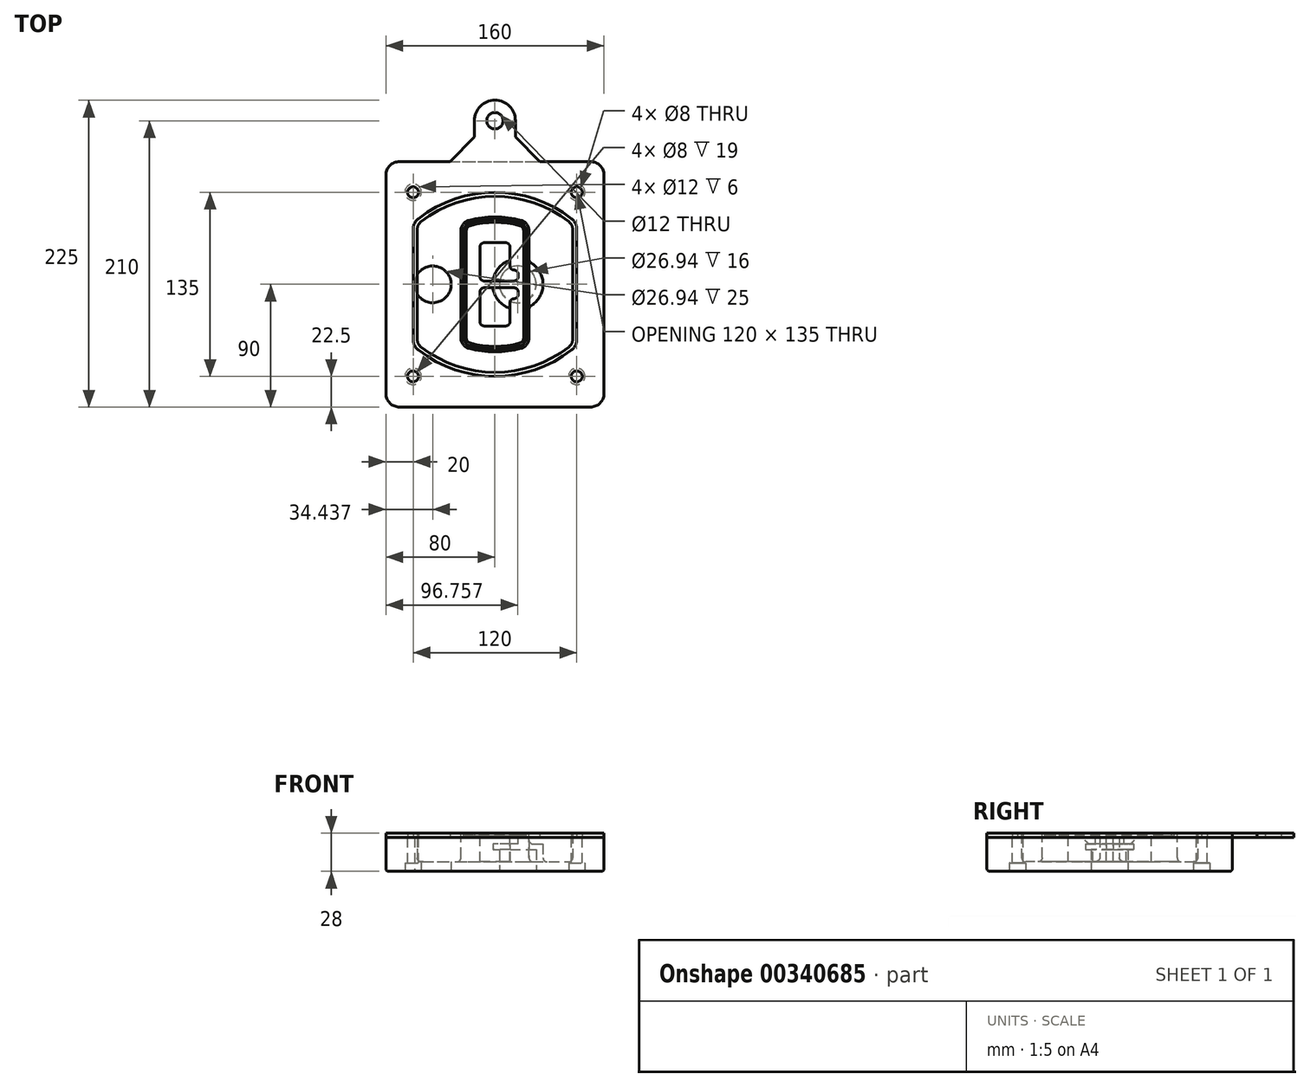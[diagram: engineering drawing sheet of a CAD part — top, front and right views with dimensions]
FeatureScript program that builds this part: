
annotation { "Feature Type Name" : "Feature", "Feature Type Description" : "" }
export const myFeature = defineFeature(function(context is Context, id is Id, definition is map)
    precondition{}
    {
        {
            var Q0;
            Q0=qCreatedBy(makeId("Top.planeOp"),FACE);
            var sketch = newSketch(context, id + "F0", { "sketchPlane" : qUnion([Q0])});
            skPoint(sketch, "E0.rect.middle", {"position": v(0, 0) * mm});
            skLineSegment(sketch, "E1.bottom", {"start": v(-70, -90) * mm, "end": v(70, -90) * mm});
            skLineSegment(sketch, "E1.top", {"start": v(-70, 90) * mm, "end": v(70, 90) * mm});
            skLineSegment(sketch, "E1.left", {"start": v(-80, -80) * mm, "end": v(-80, 80) * mm});
            skLineSegment(sketch, "E1.right", {"start": v(80, -80) * mm, "end": v(80, 80) * mm});
            skLineSegment(sketch, "E2", {"start": v(-80, 90) * mm, "end": v(80, -90) * mm, "construction": true});
            skLineSegment(sketch, "E3", {"start": v(80, 90) * mm, "end": v(-80, -90) * mm, "construction": true});
            skCircle(sketch, "E4", {"center": v(-60, 67.5) * mm, "radius": 4 * mm});
            skCircle(sketch, "E5", {"center": v(60, 67.5) * mm, "radius": 4 * mm});
            skCircle(sketch, "E6", {"center": v(60, -67.5) * mm, "radius": 4 * mm});
            skCircle(sketch, "E7", {"center": v(-60, -67.5) * mm, "radius": 4 * mm});
            skLineSegment(sketch, "E8", {"start": v(-60, 67.5) * mm, "end": v(60, 67.5) * mm, "construction": true});
            skLineSegment(sketch, "E9", {"start": v(60, 67.5) * mm, "end": v(60, -67.5) * mm, "construction": true});
            skLineSegment(sketch, "E10", {"start": v(60, -67.5) * mm, "end": v(-60, -67.5) * mm, "construction": true});
            skLineSegment(sketch, "E11", {"start": v(-60, -67.5) * mm, "end": v(-60, 67.5) * mm, "construction": true});
            skLineSegment(sketch, "E12", {"start": v(-60, 40.3) * mm, "end": v(-60, -40.3) * mm});
            skLineSegment(sketch, "E13", {"start": v(60, 40.3) * mm, "end": v(60, -40.3) * mm});
            skArc(sketch, "E14", {"start": v(56.15, 48.18) * mm, "mid": v(0, 67.5) * mm, "end": v(-56.15, 48.18) * mm});
            skArc(sketch, "E15", {"start": v(-56.15, -48.18) * mm, "mid": v(0, -67.5) * mm, "end": v(56.15, -48.18) * mm});
            skLineSegment(sketch, "E16", {"start": v(-60, 0) * mm, "end": v(60, 0) * mm, "construction": true});
            skPoint(sketch, "E17.visualSharp", {"position": v(-60, -45) * mm});
            skArc(sketch, "E17.filletArc", {"start": v(-60, -40.3) * mm, "mid": v(-58.99, -44.68) * mm, "end": v(-56.15, -48.18) * mm});
            skPoint(sketch, "E18.visualSharp", {"position": v(-60, 45) * mm});
            skArc(sketch, "E18.filletArc", {"start": v(-56.15, 48.18) * mm, "mid": v(-58.99, 44.68) * mm, "end": v(-60, 40.3) * mm});
            skPoint(sketch, "E19.visualSharp", {"position": v(60, 45) * mm});
            skArc(sketch, "E19.filletArc", {"start": v(60, 40.3) * mm, "mid": v(58.99, 44.68) * mm, "end": v(56.15, 48.18) * mm});
            skPoint(sketch, "E20.visualSharp", {"position": v(60, -45) * mm});
            skArc(sketch, "E20.filletArc", {"start": v(56.15, -48.18) * mm, "mid": v(58.99, -44.68) * mm, "end": v(60, -40.3) * mm});
            skPoint(sketch, "E21.visualSharp", {"position": v(-80, 90) * mm});
            skArc(sketch, "E21.filletArc", {"start": v(-70, 90) * mm, "mid": v(-77.07, 87.07) * mm, "end": v(-80, 80) * mm});
            skPoint(sketch, "E22.visualSharp", {"position": v(80, 90) * mm});
            skArc(sketch, "E22.filletArc", {"start": v(80, 80) * mm, "mid": v(77.07, 87.07) * mm, "end": v(70, 90) * mm});
            skPoint(sketch, "E23.visualSharp", {"position": v(80, -90) * mm});
            skArc(sketch, "E23.filletArc", {"start": v(70, -90) * mm, "mid": v(77.07, -87.07) * mm, "end": v(80, -80) * mm});
            skPoint(sketch, "E24.visualSharp", {"position": v(-80, -90) * mm});
            skArc(sketch, "E24.filletArc", {"start": v(-80, -80) * mm, "mid": v(-77.07, -87.07) * mm, "end": v(-70, -90) * mm});
            skArc(sketch, "E25.0", {"start": v(57, 40.3) * mm, "mid": v(56.3, 43.36) * mm, "end": v(54.3, 45.81) * mm});
            skLineSegment(sketch, "E25.1", {"start": v(57, 40.3) * mm, "end": v(57, -40.3) * mm});
            skArc(sketch, "E25.2", {"start": v(54.3, -45.81) * mm, "mid": v(56.3, -43.36) * mm, "end": v(57, -40.3) * mm});
            skArc(sketch, "E25.3", {"start": v(-54.3, -45.81) * mm, "mid": v(0, -64.5) * mm, "end": v(54.3, -45.81) * mm});
            skArc(sketch, "E25.4", {"start": v(-57, -40.3) * mm, "mid": v(-56.3, -43.36) * mm, "end": v(-54.3, -45.81) * mm});
            skArc(sketch, "E25.5", {"start": v(54.3, 45.81) * mm, "mid": v(0, 64.5) * mm, "end": v(-54.3, 45.81) * mm});
            skLineSegment(sketch, "E25.6", {"start": v(-57, 40.3) * mm, "end": v(-57, -40.3) * mm});
            skArc(sketch, "E25.7", {"start": v(-54.3, 45.81) * mm, "mid": v(-56.3, 43.36) * mm, "end": v(-57, 40.3) * mm});
            skArc(sketch, "E26.0", {"start": v(-58.62, 51.33) * mm, "mid": v(-62.58, 46.43) * mm, "end": v(-64, 40.3) * mm});
            skArc(sketch, "E26.1", {"start": v(58.62, 51.33) * mm, "mid": v(0, 71.5) * mm, "end": v(-58.62, 51.33) * mm});
            skArc(sketch, "E26.2", {"start": v(64, 40.3) * mm, "mid": v(62.58, 46.43) * mm, "end": v(58.62, 51.33) * mm});
            skLineSegment(sketch, "E26.3", {"start": v(64, 40.3) * mm, "end": v(64, -40.3) * mm});
            skArc(sketch, "E26.4", {"start": v(58.62, -51.33) * mm, "mid": v(62.58, -46.43) * mm, "end": v(64, -40.3) * mm});
            skLineSegment(sketch, "E26.5", {"start": v(-64, 40.3) * mm, "end": v(-64, -40.3) * mm});
            skArc(sketch, "E26.6", {"start": v(-58.62, -51.33) * mm, "mid": v(0, -71.5) * mm, "end": v(58.62, -51.33) * mm});
            skArc(sketch, "E26.7", {"start": v(-64, -40.3) * mm, "mid": v(-62.58, -46.43) * mm, "end": v(-58.62, -51.33) * mm});
            skSolve(sketch);
        }
        {
            var Q0;
            Q0=makeQuery(id+"F0.imprint","IMPRINT",FACE,{"disambiguationData":[TD([[makeQuery(id+"F0.imprint","IMPRINT",EDGE,{"derivedFrom":sQuery(id+"F0.wireOp",EDGE,"E1.bottom")}),1.0]])]});
            var Q1;
            Q1=makeQuery(id+"F0.imprint","IMPRINT",FACE,{"disambiguationData":[TD([[makeQuery(id+"F0.imprint","IMPRINT",EDGE,{"derivedFrom":sQuery(id+"F0.wireOp",EDGE,"E12")}),1.0]])]});
            var Q2;
            Q2=makeQuery(id+"F0.imprint","IMPRINT",FACE,{"disambiguationData":[TD([[makeQuery(id+"F0.imprint","IMPRINT",EDGE,{"derivedFrom":sQuery(id+"F0.wireOp",EDGE,"E25.0")}),1.0]])]});
            var Q3;
            Q3=makeQuery(id+"F0.imprint","IMPRINT",FACE,{"disambiguationData":[TD([[makeQuery(id+"F0.imprint","IMPRINT",EDGE,{"derivedFrom":sQuery(id+"F0.wireOp",EDGE,"E12")}),-1.0]])]});
            extrude(context, id + "F1", {"entities" : qUnion([Q0, Q1, Q2, Q3]), "oppositeDirection" : true, "depth" : 25 * mm});
        }
        {
            var Q0;
            Q0=makeQuery(id+"F0.imprint","IMPRINT",FACE,{"disambiguationData":[TD([[makeQuery(id+"F0.imprint","IMPRINT",EDGE,{"derivedFrom":sQuery(id+"F0.wireOp",EDGE,"E12")}),1.0]])]});
            extrude(context, id + "F2", {"entities" : qUnion([Q0]), "operationType" : NewBodyOperationType.ADD, "depth" : 3 * mm});
        }
        {
            var Q0;
            Q0=makeQuery(id+"F0.imprint","IMPRINT",FACE,{"disambiguationData":[TD([[makeQuery(id+"F0.imprint","IMPRINT",EDGE,{"derivedFrom":sQuery(id+"F0.wireOp",EDGE,"E25.0")}),1.0]])]});
            extrude(context, id + "F3", {"entities" : qUnion([Q0]), "operationType" : NewBodyOperationType.REMOVE, "oppositeDirection" : true, "depth" : 18 * mm});
        }
        {
            var Q0;
            Q0=makeQuery(id+"F2.opExtrude","CAP_FACE",FACE,{"disambiguationData":[OSD([sQuery(id+"F0.wireOp",EDGE,"E12"),sQuery(id+"F0.wireOp",EDGE,"E13"),sQuery(id+"F0.wireOp",EDGE,"E14"),sQuery(id+"F0.wireOp",EDGE,"E15"),sQuery(id+"F0.wireOp",EDGE,"E17.filletArc"),sQuery(id+"F0.wireOp",EDGE,"E18.filletArc"),sQuery(id+"F0.wireOp",EDGE,"E19.filletArc"),sQuery(id+"F0.wireOp",EDGE,"E20.filletArc"),sQuery(id+"F0.wireOp",EDGE,"E25.0"),sQuery(id+"F0.wireOp",EDGE,"E25.1"),sQuery(id+"F0.wireOp",EDGE,"E25.2"),sQuery(id+"F0.wireOp",EDGE,"E25.3"),sQuery(id+"F0.wireOp",EDGE,"E25.4"),sQuery(id+"F0.wireOp",EDGE,"E25.5"),sQuery(id+"F0.wireOp",EDGE,"E25.6"),sQuery(id+"F0.wireOp",EDGE,"E25.7")])],"isStart":false});
            var sketch = newSketch(context, id + "F4", { "sketchPlane" : qUnion([Q0])});
            skArc(sketch, "E27.0", {"start": v(-19.08, -46.97) * mm, "mid": v(0, -49.5) * mm, "end": v(19.08, -46.97) * mm});
            skArc(sketch, "E28.0", {"start": v(19.08, 46.97) * mm, "mid": v(0, 49.5) * mm, "end": v(-19.08, 46.97) * mm});
            skLineSegment(sketch, "E29", {"start": v(-25, 39.25) * mm, "end": v(-25, -39.25) * mm});
            skLineSegment(sketch, "E30", {"start": v(25, 39.25) * mm, "end": v(25, -39.25) * mm});
            skLineSegment(sketch, "E31", {"start": v(-25, 45.1) * mm, "end": v(25, 45.1) * mm, "construction": true});
            skLineSegment(sketch, "E32", {"start": v(-25, -45.1) * mm, "end": v(25, -45.1) * mm, "construction": true});
            skPoint(sketch, "E33.visualSharp", {"position": v(-25, 45.1) * mm});
            skArc(sketch, "E33.filletArc", {"start": v(-19.08, 46.97) * mm, "mid": v(-23.35, 44.11) * mm, "end": v(-25, 39.25) * mm});
            skPoint(sketch, "E34.visualSharp", {"position": v(25, 45.1) * mm});
            skArc(sketch, "E34.filletArc", {"start": v(25, 39.25) * mm, "mid": v(23.35, 44.11) * mm, "end": v(19.08, 46.97) * mm});
            skPoint(sketch, "E35.visualSharp", {"position": v(25, -45.1) * mm});
            skArc(sketch, "E35.filletArc", {"start": v(19.08, -46.97) * mm, "mid": v(23.35, -44.11) * mm, "end": v(25, -39.25) * mm});
            skPoint(sketch, "E36.visualSharp", {"position": v(-25, -45.1) * mm});
            skArc(sketch, "E36.filletArc", {"start": v(-25, -39.25) * mm, "mid": v(-23.35, -44.11) * mm, "end": v(-19.08, -46.97) * mm});
            skArc(sketch, "E37.0", {"start": v(54.3, 45.81) * mm, "mid": v(0, 64.5) * mm, "end": v(-54.3, 45.81) * mm});
            skArc(sketch, "E37.1", {"start": v(-54.3, 45.81) * mm, "mid": v(-56.3, 43.36) * mm, "end": v(-57, 40.3) * mm});
            skLineSegment(sketch, "E37.2", {"start": v(-57, 40.3) * mm, "end": v(-57, -40.3) * mm});
            skArc(sketch, "E37.3", {"start": v(-57, -40.3) * mm, "mid": v(-56.3, -43.36) * mm, "end": v(-54.3, -45.81) * mm});
            skArc(sketch, "E37.4", {"start": v(-54.3, -45.81) * mm, "mid": v(0, -64.5) * mm, "end": v(54.3, -45.81) * mm});
            skArc(sketch, "E37.5", {"start": v(54.3, -45.81) * mm, "mid": v(56.3, -43.36) * mm, "end": v(57, -40.3) * mm});
            skLineSegment(sketch, "E37.6", {"start": v(57, 40.3) * mm, "end": v(57, -40.3) * mm});
            skArc(sketch, "E37.7", {"start": v(57, 40.3) * mm, "mid": v(56.3, 43.36) * mm, "end": v(54.3, 45.81) * mm});
            skLineSegment(sketch, "E38.0", {"start": v(23, 39.25) * mm, "end": v(23, -39.25) * mm});
            skArc(sketch, "E38.1", {"start": v(18.56, -45.04) * mm, "mid": v(21.76, -42.9) * mm, "end": v(23, -39.25) * mm});
            skArc(sketch, "E38.2", {"start": v(-18.56, -45.04) * mm, "mid": v(0, -47.5) * mm, "end": v(18.56, -45.04) * mm});
            skArc(sketch, "E38.3", {"start": v(-23, -39.25) * mm, "mid": v(-21.76, -42.9) * mm, "end": v(-18.56, -45.04) * mm});
            skLineSegment(sketch, "E38.4", {"start": v(-23, 39.25) * mm, "end": v(-23, -39.25) * mm});
            skArc(sketch, "E38.5", {"start": v(23, 39.25) * mm, "mid": v(21.76, 42.9) * mm, "end": v(18.56, 45.04) * mm});
            skArc(sketch, "E38.6", {"start": v(-18.56, 45.04) * mm, "mid": v(-21.76, 42.9) * mm, "end": v(-23, 39.25) * mm});
            skArc(sketch, "E38.7", {"start": v(18.56, 45.04) * mm, "mid": v(0, 47.5) * mm, "end": v(-18.56, 45.04) * mm});
            skArc(sketch, "E39.0", {"start": v(21, 39.25) * mm, "mid": v(20.18, 41.68) * mm, "end": v(18.04, 43.1) * mm});
            skLineSegment(sketch, "E39.1", {"start": v(21, 39.25) * mm, "end": v(21, -39.25) * mm});
            skArc(sketch, "E39.2", {"start": v(18.04, -43.1) * mm, "mid": v(20.18, -41.68) * mm, "end": v(21, -39.25) * mm});
            skArc(sketch, "E39.3", {"start": v(-18.04, -43.1) * mm, "mid": v(0, -45.5) * mm, "end": v(18.04, -43.1) * mm});
            skArc(sketch, "E39.4", {"start": v(-21, -39.25) * mm, "mid": v(-20.18, -41.68) * mm, "end": v(-18.04, -43.1) * mm});
            skArc(sketch, "E39.5", {"start": v(18.04, 43.1) * mm, "mid": v(0, 45.5) * mm, "end": v(-18.04, 43.1) * mm});
            skLineSegment(sketch, "E39.6", {"start": v(-21, 39.25) * mm, "end": v(-21, -39.25) * mm});
            skArc(sketch, "E39.7", {"start": v(-18.04, 43.1) * mm, "mid": v(-20.18, 41.68) * mm, "end": v(-21, 39.25) * mm});
            skLineSegment(sketch, "E40", {"start": v(-25, 0) * mm, "end": v(25, 0) * mm, "construction": true});
            skLineSegment(sketch, "E41", {"start": v(-11, 5.5) * mm, "end": v(-11, 27.5) * mm});
            skLineSegment(sketch, "E42", {"start": v(-8, 30.5) * mm, "end": v(8, 30.5) * mm});
            skLineSegment(sketch, "E43", {"start": v(11, 27.5) * mm, "end": v(11, 13.5) * mm});
            skLineSegment(sketch, "E44", {"start": v(14, 10.5) * mm, "end": v(14, 10.5) * mm});
            skLineSegment(sketch, "E45", {"start": v(17, 7.5) * mm, "end": v(17, 5.5) * mm});
            skLineSegment(sketch, "E46", {"start": v(14, 2.5) * mm, "end": v(-8, 2.5) * mm});
            skPoint(sketch, "E47.visualSharp", {"position": v(-11, 30.5) * mm});
            skArc(sketch, "E47.filletArc", {"start": v(-8, 30.5) * mm, "mid": v(-10.12, 29.62) * mm, "end": v(-11, 27.5) * mm});
            skPoint(sketch, "E48.visualSharp", {"position": v(11, 30.5) * mm});
            skArc(sketch, "E48.filletArc", {"start": v(11, 27.5) * mm, "mid": v(10.12, 29.62) * mm, "end": v(8, 30.5) * mm});
            skPoint(sketch, "E49.visualSharp", {"position": v(11, 10.5) * mm});
            skArc(sketch, "E49.filletArc", {"start": v(11, 13.5) * mm, "mid": v(11.88, 11.38) * mm, "end": v(14, 10.5) * mm});
            skPoint(sketch, "E50.visualSharp", {"position": v(17, 10.5) * mm});
            skArc(sketch, "E50.filletArc", {"start": v(17, 7.5) * mm, "mid": v(16.12, 9.62) * mm, "end": v(14, 10.5) * mm});
            skPoint(sketch, "E51.visualSharp", {"position": v(17, 2.5) * mm});
            skArc(sketch, "E51.filletArc", {"start": v(14, 2.5) * mm, "mid": v(16.12, 3.38) * mm, "end": v(17, 5.5) * mm});
            skPoint(sketch, "E52.visualSharp", {"position": v(-11, 2.5) * mm});
            skArc(sketch, "E52.filletArc", {"start": v(-11, 5.5) * mm, "mid": v(-10.12, 3.38) * mm, "end": v(-8, 2.5) * mm});
            skLineSegment(sketch, "E53.0.MirrorCS", {"start": v(14, -2.5) * mm, "end": v(-8, -2.5) * mm});
            skArc(sketch, "E54.0.MirrorCS", {"start": v(-11, -5.5) * mm, "mid": v(-10.12, -3.38) * mm, "end": v(-8, -2.5) * mm});
            skLineSegment(sketch, "E55.0.MirrorCS", {"start": v(-11, -5.5) * mm, "end": v(-11, -27.5) * mm});
            skArc(sketch, "E56.0.MirrorCS", {"start": v(-8, -30.5) * mm, "mid": v(-10.12, -29.62) * mm, "end": v(-11, -27.5) * mm});
            skLineSegment(sketch, "E57.0.MirrorCS", {"start": v(-8, -30.5) * mm, "end": v(8, -30.5) * mm});
            skArc(sketch, "E58.0.MirrorCS", {"start": v(11, -27.5) * mm, "mid": v(10.12, -29.62) * mm, "end": v(8, -30.5) * mm});
            skLineSegment(sketch, "E59.0.MirrorCS", {"start": v(11, -27.5) * mm, "end": v(11, -13.5) * mm});
            skArc(sketch, "E60.0.MirrorCS", {"start": v(11, -13.5) * mm, "mid": v(11.88, -11.38) * mm, "end": v(14, -10.5) * mm});
            skArc(sketch, "E61.0.MirrorCS", {"start": v(17, -7.5) * mm, "mid": v(16.12, -9.62) * mm, "end": v(14, -10.5) * mm});
            skLineSegment(sketch, "E62.0.MirrorCS", {"start": v(17, -7.5) * mm, "end": v(17, -5.5) * mm});
            skArc(sketch, "E63.0.MirrorCS", {"start": v(14, -2.5) * mm, "mid": v(16.12, -3.38) * mm, "end": v(17, -5.5) * mm});
            skSolve(sketch);
        }
        {
            var Q0;
            Q0=makeQuery(id+"F4.imprint","IMPRINT",FACE,{"disambiguationData":[TD([[makeQuery(id+"F4.imprint","IMPRINT",EDGE,{"derivedFrom":sQuery(id+"F4.wireOp",EDGE,"E27.0")}),1.0]])]});
            var Q1;
            Q1=makeQuery(id+"F4.imprint","IMPRINT",FACE,{"disambiguationData":[TD([[makeQuery(id+"F4.imprint","IMPRINT",EDGE,{"derivedFrom":sQuery(id+"F4.wireOp",EDGE,"E38.0")}),-1.0]])]});
            var Q2;
            Q2=makeQuery(id+"F4.imprint","IMPRINT",FACE,{"disambiguationData":[TD([[makeQuery(id+"F4.imprint","IMPRINT",EDGE,{"derivedFrom":sQuery(id+"F4.wireOp",EDGE,"E39.0")}),1.0]])]});
            extrude(context, id + "F5", {"entities" : qUnion([Q0, Q1, Q2]), "operationType" : NewBodyOperationType.ADD, "endBound" : BoundingType.UP_TO_NEXT, "oppositeDirection" : true, "depth" : 25 * mm});
        }
        {
            var Q0;
            Q0=makeQuery(id+"F4.imprint","IMPRINT",FACE,{"disambiguationData":[TD([[makeQuery(id+"F4.imprint","IMPRINT",EDGE,{"derivedFrom":sQuery(id+"F4.wireOp",EDGE,"E38.0")}),-1.0]])]});
            extrude(context, id + "F6", {"entities" : qUnion([Q0]), "operationType" : NewBodyOperationType.REMOVE, "oppositeDirection" : true, "depth" : 2 * mm});
        }
        {
            var Q0;
            Q0=makeQuery(id+"F1.opExtrude","CAP_FACE",FACE,{"disambiguationData":[OSD([sQuery(id+"F0.wireOp",EDGE,"E1.bottom"),sQuery(id+"F0.wireOp",EDGE,"E1.top"),sQuery(id+"F0.wireOp",EDGE,"E1.left"),sQuery(id+"F0.wireOp",EDGE,"E1.right"),sQuery(id+"F0.wireOp",EDGE,"E4"),sQuery(id+"F0.wireOp",EDGE,"E5"),sQuery(id+"F0.wireOp",EDGE,"E6"),sQuery(id+"F0.wireOp",EDGE,"E7"),sQuery(id+"F0.wireOp",EDGE,"E21.filletArc"),sQuery(id+"F0.wireOp",EDGE,"E22.filletArc"),sQuery(id+"F0.wireOp",EDGE,"E23.filletArc"),sQuery(id+"F0.wireOp",EDGE,"E24.filletArc")])],"isStart":false});
            var sketch = newSketch(context, id + "F7", { "sketchPlane" : qUnion([Q0])});
            skCircle(sketch, "E64", {"center": v(16.76, 0) * mm, "radius": 13.47 * mm});
            skCircle(sketch, "E65", {"center": v(-45.56, 0) * mm, "radius": 13.47 * mm});
            skLineSegment(sketch, "E66", {"start": v(80, 0) * mm, "end": v(-80, 0) * mm});
            skCircle(sketch, "E67", {"center": v(16.76, 0) * mm, "radius": 18.47 * mm});
            skCircle(sketch, "E68", {"center": v(60, -67.5) * mm, "radius": 6 * mm});
            skCircle(sketch, "E69", {"center": v(-60, -67.5) * mm, "radius": 6 * mm});
            skCircle(sketch, "E70", {"center": v(-60, 67.5) * mm, "radius": 6 * mm});
            skCircle(sketch, "E71", {"center": v(60, 67.5) * mm, "radius": 6 * mm});
            skSolve(sketch);
        }
        {
            var Q0;
            {var subQ1=sQuery(id+"F7.wireOp",EDGE,"E66");var subQ4=sQuery(id+"F7.wireOp",EDGE,"E64");var subQ6=makeQuery(id+"F7.imprint","INTERSECT",VERTEX,{"disambiguationData":[OD(0.0)],"derivedFrom":[subQ4,subQ1]});Q0=makeQuery(id+"F7.imprint","IMPRINT",FACE,{"disambiguationData":[TD([[makeQuery(id+"F7.imprint","IMPRINT",EDGE,{"disambiguationData":[TD([[subQ6,-1.0]])],"derivedFrom":subQ4}),-1.0]])]});}
            var Q1;
            {var subQ0=sQuery(id+"F7.wireOp",EDGE,"E66");var subQ1=sQuery(id+"F7.wireOp",EDGE,"E64");var subQ3=makeQuery(id+"F7.imprint","INTERSECT",VERTEX,{"disambiguationData":[OD(0.0)],"derivedFrom":[subQ1,subQ0]});Q1=makeQuery(id+"F7.imprint","IMPRINT",FACE,{"disambiguationData":[TD([[makeQuery(id+"F7.imprint","IMPRINT",EDGE,{"disambiguationData":[TD([[subQ3,-1.0]])],"derivedFrom":subQ1}),1.0]])]});}
            var Q2;
            {var subQ0=sQuery(id+"F7.wireOp",EDGE,"E66");var subQ1=sQuery(id+"F7.wireOp",EDGE,"E64");var subQ3=makeQuery(id+"F7.imprint","INTERSECT",VERTEX,{"disambiguationData":[OD(0.0)],"derivedFrom":[subQ1,subQ0]});Q2=makeQuery(id+"F7.imprint","IMPRINT",FACE,{"disambiguationData":[TD([[makeQuery(id+"F7.imprint","IMPRINT",EDGE,{"disambiguationData":[TD([[subQ3,1.0]])],"derivedFrom":subQ1}),1.0]])]});}
            var Q3;
            {var subQ1=sQuery(id+"F7.wireOp",EDGE,"E66");var subQ4=sQuery(id+"F7.wireOp",EDGE,"E64");var subQ6=makeQuery(id+"F7.imprint","INTERSECT",VERTEX,{"disambiguationData":[OD(0.0)],"derivedFrom":[subQ4,subQ1]});Q3=makeQuery(id+"F7.imprint","IMPRINT",FACE,{"disambiguationData":[TD([[makeQuery(id+"F7.imprint","IMPRINT",EDGE,{"disambiguationData":[TD([[subQ6,1.0]])],"derivedFrom":subQ4}),-1.0]])]});}
            extrude(context, id + "F8", {"entities" : qUnion([Q0, Q1, Q2, Q3]), "operationType" : NewBodyOperationType.ADD, "oppositeDirection" : true, "depth" : 20 * mm});
        }
        {
            var Q0;
            {var subQ0=sQuery(id+"F7.wireOp",EDGE,"E66");var subQ1=sQuery(id+"F7.wireOp",EDGE,"E64");var subQ3=makeQuery(id+"F7.imprint","INTERSECT",VERTEX,{"disambiguationData":[OD(0.0)],"derivedFrom":[subQ1,subQ0]});Q0=makeQuery(id+"F7.imprint","IMPRINT",FACE,{"disambiguationData":[TD([[makeQuery(id+"F7.imprint","IMPRINT",EDGE,{"disambiguationData":[TD([[subQ3,-1.0]])],"derivedFrom":subQ1}),1.0]])]});}
            var Q1;
            {var subQ0=sQuery(id+"F7.wireOp",EDGE,"E66");var subQ1=sQuery(id+"F7.wireOp",EDGE,"E64");var subQ3=makeQuery(id+"F7.imprint","INTERSECT",VERTEX,{"disambiguationData":[OD(0.0)],"derivedFrom":[subQ1,subQ0]});Q1=makeQuery(id+"F7.imprint","IMPRINT",FACE,{"disambiguationData":[TD([[makeQuery(id+"F7.imprint","IMPRINT",EDGE,{"disambiguationData":[TD([[subQ3,1.0]])],"derivedFrom":subQ1}),1.0]])]});}
            extrude(context, id + "F9", {"entities" : qUnion([Q0, Q1]), "operationType" : NewBodyOperationType.REMOVE, "oppositeDirection" : true, "depth" : 16 * mm});
        }
        {
            var Q0;
            {var subQ0=sQuery(id+"F7.wireOp",EDGE,"E66");var subQ1=sQuery(id+"F7.wireOp",EDGE,"E65");var subQ3=makeQuery(id+"F7.imprint","INTERSECT",VERTEX,{"disambiguationData":[OD(0.0)],"derivedFrom":[subQ1,subQ0]});Q0=makeQuery(id+"F7.imprint","IMPRINT",FACE,{"disambiguationData":[TD([[makeQuery(id+"F7.imprint","IMPRINT",EDGE,{"disambiguationData":[TD([[subQ3,-1.0]])],"derivedFrom":subQ1}),1.0]])]});}
            var Q1;
            {var subQ0=sQuery(id+"F7.wireOp",EDGE,"E66");var subQ1=sQuery(id+"F7.wireOp",EDGE,"E65");var subQ3=makeQuery(id+"F7.imprint","INTERSECT",VERTEX,{"disambiguationData":[OD(0.0)],"derivedFrom":[subQ1,subQ0]});Q1=makeQuery(id+"F7.imprint","IMPRINT",FACE,{"disambiguationData":[TD([[makeQuery(id+"F7.imprint","IMPRINT",EDGE,{"disambiguationData":[TD([[subQ3,1.0]])],"derivedFrom":subQ1}),1.0]])]});}
            extrude(context, id + "F10", {"entities" : qUnion([Q0, Q1]), "operationType" : NewBodyOperationType.REMOVE, "oppositeDirection" : true, "depth" : 25 * mm});
        }
        {
            var Q0;
            Q0=makeQuery(id+"F7.imprint","IMPRINT",FACE,{"disambiguationData":[TD([[makeQuery(id+"F7.imprint","IMPRINT",EDGE,{"derivedFrom":sQuery(id+"F7.wireOp",EDGE,"E68")}),1.0]])]});
            var Q1;
            Q1=makeQuery(id+"F7.imprint","IMPRINT",FACE,{"disambiguationData":[TD([[makeQuery(id+"F7.imprint","IMPRINT",EDGE,{"derivedFrom":makeQuery(id+"F1.opExtrude","CAP_EDGE",EDGE,{"disambiguationData":[OSD([sQuery(id+"F0.wireOp",EDGE,"E5")])],"isStart":false})}),-1.0]])]});
            var Q2;
            Q2=makeQuery(id+"F7.imprint","IMPRINT",FACE,{"disambiguationData":[TD([[makeQuery(id+"F7.imprint","IMPRINT",EDGE,{"derivedFrom":sQuery(id+"F7.wireOp",EDGE,"E69")}),1.0]])]});
            var Q3;
            Q3=makeQuery(id+"F7.imprint","IMPRINT",FACE,{"disambiguationData":[TD([[makeQuery(id+"F7.imprint","IMPRINT",EDGE,{"derivedFrom":makeQuery(id+"F1.opExtrude","CAP_EDGE",EDGE,{"disambiguationData":[OSD([sQuery(id+"F0.wireOp",EDGE,"E4")])],"isStart":false})}),-1.0]])]});
            var Q4;
            Q4=makeQuery(id+"F7.imprint","IMPRINT",FACE,{"disambiguationData":[TD([[makeQuery(id+"F7.imprint","IMPRINT",EDGE,{"derivedFrom":sQuery(id+"F7.wireOp",EDGE,"E70")}),1.0]])]});
            var Q5;
            Q5=makeQuery(id+"F7.imprint","IMPRINT",FACE,{"disambiguationData":[TD([[makeQuery(id+"F7.imprint","IMPRINT",EDGE,{"derivedFrom":makeQuery(id+"F1.opExtrude","CAP_EDGE",EDGE,{"disambiguationData":[OSD([sQuery(id+"F0.wireOp",EDGE,"E7")])],"isStart":false})}),-1.0]])]});
            var Q6;
            Q6=makeQuery(id+"F7.imprint","IMPRINT",FACE,{"disambiguationData":[TD([[makeQuery(id+"F7.imprint","IMPRINT",EDGE,{"derivedFrom":sQuery(id+"F7.wireOp",EDGE,"E71")}),1.0]])]});
            var Q7;
            Q7=makeQuery(id+"F7.imprint","IMPRINT",FACE,{"disambiguationData":[TD([[makeQuery(id+"F7.imprint","IMPRINT",EDGE,{"derivedFrom":makeQuery(id+"F1.opExtrude","CAP_EDGE",EDGE,{"disambiguationData":[OSD([sQuery(id+"F0.wireOp",EDGE,"E6")])],"isStart":false})}),-1.0]])]});
            extrude(context, id + "F11", {"entities" : qUnion([Q0, Q1, Q2, Q3, Q4, Q5, Q6, Q7]), "operationType" : NewBodyOperationType.REMOVE, "oppositeDirection" : true, "depth" : 6 * mm});
        }
        {
            var Q0;
            Q0=makeQuery(id+"F9.boolean.opBoolean","COPY",FACE,{"derivedFrom":makeQuery(id+"F9.opExtrude","CAP_FACE",FACE,{"disambiguationData":[OSD([sQuery(id+"F7.wireOp",EDGE,"E64")])],"isStart":false})});
            var sketch = newSketch(context, id + "F12", { "sketchPlane" : qUnion([Q0])});
            skArc(sketch, "E72.0", {"start": v(11, 17.55) * mm, "mid": v(2.57, 11.82) * mm, "end": v(-1.54, 2.5) * mm});
            skArc(sketch, "E72.1", {"start": v(-1.54, -2.5) * mm, "mid": v(2.57, -11.82) * mm, "end": v(11, -17.55) * mm});
            skLineSegment(sketch, "E73", {"start": v(-1.54, -2.5) * mm, "end": v(14, -2.5) * mm});
            skLineSegment(sketch, "E74.0", {"start": v(14, 2.5) * mm, "end": v(-1.54, 2.5) * mm});
            skArc(sketch, "E74.1", {"start": v(14, 2.5) * mm, "mid": v(16.12, 3.38) * mm, "end": v(17, 5.5) * mm});
            skLineSegment(sketch, "E74.2", {"start": v(17, 7.5) * mm, "end": v(17, 5.5) * mm});
            skArc(sketch, "E74.3", {"start": v(17, 7.5) * mm, "mid": v(16.12, 9.62) * mm, "end": v(14, 10.5) * mm});
            skArc(sketch, "E74.4", {"start": v(11, 13.5) * mm, "mid": v(11.88, 11.38) * mm, "end": v(14, 10.5) * mm});
            skLineSegment(sketch, "E74.5", {"start": v(11, 17.55) * mm, "end": v(11, 13.5) * mm});
            skLineSegment(sketch, "E74.7", {"start": v(14, -2.5) * mm, "end": v(-1.54, -2.5) * mm});
            skArc(sketch, "E74.8", {"start": v(14, -2.5) * mm, "mid": v(16.12, -3.38) * mm, "end": v(17, -5.5) * mm});
            skLineSegment(sketch, "E74.9", {"start": v(17, -7.5) * mm, "end": v(17, -5.5) * mm});
            skArc(sketch, "E74.10", {"start": v(17, -7.5) * mm, "mid": v(16.12, -9.62) * mm, "end": v(14, -10.5) * mm});
            skArc(sketch, "E74.11", {"start": v(11, -13.5) * mm, "mid": v(11.88, -11.38) * mm, "end": v(14, -10.5) * mm});
            skLineSegment(sketch, "E74.12", {"start": v(11, -17.55) * mm, "end": v(11, -13.5) * mm});
            skPoint(sketch, "E75.orphan", {"position": v(11, -27.5) * mm});
            skPoint(sketch, "E76.orphan", {"position": v(-8, -2.5) * mm});
            skPoint(sketch, "E77.orphan", {"position": v(-8, 2.5) * mm});
            skPoint(sketch, "E78.orphan", {"position": v(11, 27.5) * mm});
            skSolve(sketch);
        }
        {
            var Q0;
            {var subQ7=sQuery(id+"F12.wireOp",EDGE,"E72.0");var subQ14=sQuery(id+"F12.wireOp",EDGE,"E72.1");var subQ16=sQuery(id+"F12.wireOp",EDGE,"E74.1");var subQ18=sQuery(id+"F12.wireOp",EDGE,"E74.8");Q0=qUnion([makeQuery(id+"F12.imprint","IMPRINT",FACE,{"disambiguationData":[TD([[makeQuery(id+"F12.imprint","IMPRINT",EDGE,{"derivedFrom":subQ7}),1.0]])]}),makeQuery(id+"F12.imprint","IMPRINT",FACE,{"disambiguationData":[TD([[makeQuery(id+"F12.imprint","IMPRINT",EDGE,{"derivedFrom":subQ14}),1.0]])]}),makeQuery(id+"F12.imprint","IMPRINT",FACE,{"disambiguationData":[TD([[makeQuery(id+"F12.imprint","IMPRINT",EDGE,{"derivedFrom":subQ16}),1.0]])]}),makeQuery(id+"F12.imprint","IMPRINT",FACE,{"disambiguationData":[TD([[makeQuery(id+"F12.imprint","IMPRINT",EDGE,{"derivedFrom":subQ18}),-1.0]])]})]);}
            var Q1;
            Q1=makeQuery(id+"F5.boolean.opBoolean","SPLIT",FACE,{"disambiguationData":[TD([makeQuery(id+"F5.opExtrude","SWEPT_FACE",FACE,{"disambiguationData":[OSD([sQuery(id+"F4.wireOp",EDGE,"E41")])]})])],"derivedFrom":makeQuery(id+"F3.boolean.opBoolean","COPY",FACE,{"derivedFrom":makeQuery(id+"F3.opExtrude","CAP_FACE",FACE,{"disambiguationData":[OSD([sQuery(id+"F0.wireOp",EDGE,"E25.0"),sQuery(id+"F0.wireOp",EDGE,"E25.1"),sQuery(id+"F0.wireOp",EDGE,"E25.2"),sQuery(id+"F0.wireOp",EDGE,"E25.3"),sQuery(id+"F0.wireOp",EDGE,"E25.4"),sQuery(id+"F0.wireOp",EDGE,"E25.5"),sQuery(id+"F0.wireOp",EDGE,"E25.6"),sQuery(id+"F0.wireOp",EDGE,"E25.7")])],"isStart":false})})});
            extrude(context, id + "F13", {"entities" : qUnion([Q0]), "operationType" : NewBodyOperationType.REMOVE, "endBound" : BoundingType.UP_TO_SURFACE, "endBoundEntityFace" : qUnion([Q1]), "depth" : 25 * mm});
        }
        {
            var Q0;
            Q0=makeQuery(id+"F3.boolean.opBoolean","COPY",EDGE,{"derivedFrom":makeQuery(id+"F3.opExtrude","CAP_EDGE",EDGE,{"disambiguationData":[OSD([sQuery(id+"F0.wireOp",EDGE,"E25.6")])],"isStart":false})});
            var Q1;
            Q1=makeQuery(id+"F8.boolean.opBoolean","INTERSECT",EDGE,{"derivedFrom":[makeQuery(id+"F5.opExtrude","SWEPT_FACE",FACE,{"disambiguationData":[OSD([sQuery(id+"F4.wireOp",EDGE,"E30")])]}),makeQuery(id+"F8.opExtrude","CAP_FACE",FACE,{"disambiguationData":[OSD([sQuery(id+"F7.wireOp",EDGE,"E67")])],"isStart":false})]});
            var Q2;
            Q2=makeQuery(id+"F8.boolean.opBoolean","INTERSECT",EDGE,{"disambiguationData":[OD(1.0)],"derivedFrom":[makeQuery(id+"F5.opExtrude","SWEPT_FACE",FACE,{"disambiguationData":[OSD([sQuery(id+"F4.wireOp",EDGE,"E30")])]}),makeQuery(id+"F8.opExtrude","SWEPT_FACE",FACE,{"disambiguationData":[OSD([sQuery(id+"F7.wireOp",EDGE,"E67")])]})]});
            var Q3;
            {var subQ0=sQuery(id+"F4.wireOp",EDGE,"E30");Q3=makeQuery(id+"F8.boolean.opBoolean","SPLIT",EDGE,{"disambiguationData":[TD([makeQuery(id+"F5.opExtrude","SWEPT_FACE",FACE,{"disambiguationData":[OSD([sQuery(id+"F4.wireOp",EDGE,"E35.filletArc")])]})])],"derivedFrom":makeQuery(id+"F5.opExtrude","CAP_EDGE",EDGE,{"disambiguationData":[OSD([subQ0])],"isStart":false})});}
            var Q4;
            {var subQ0=sQuery(id+"F0.wireOp",EDGE,"E25.7");var subQ1=sQuery(id+"F0.wireOp",EDGE,"E25.1");var subQ2=sQuery(id+"F0.wireOp",EDGE,"E25.6");var subQ3=sQuery(id+"F0.wireOp",EDGE,"E25.5");var subQ4=sQuery(id+"F0.wireOp",EDGE,"E25.4");var subQ5=sQuery(id+"F0.wireOp",EDGE,"E25.0");var subQ6=sQuery(id+"F0.wireOp",EDGE,"E25.2");var subQ7=sQuery(id+"F0.wireOp",EDGE,"E25.3");Q4=makeQuery(id+"F8.boolean.opBoolean","INTERSECT",EDGE,{"derivedFrom":[makeQuery(id+"F5.boolean.opBoolean","SPLIT",FACE,{"disambiguationData":[TD([makeQuery(id+"F2.opExtrude","SWEPT_FACE",FACE,{"disambiguationData":[OSD([subQ5])]})])],"derivedFrom":makeQuery(id+"F3.boolean.opBoolean","COPY",FACE,{"derivedFrom":makeQuery(id+"F3.opExtrude","CAP_FACE",FACE,{"disambiguationData":[OSD([subQ5,subQ1,subQ6,subQ7,subQ4,subQ3,subQ2,subQ0])],"isStart":false})})}),makeQuery(id+"F8.opExtrude","SWEPT_FACE",FACE,{"disambiguationData":[OSD([sQuery(id+"F7.wireOp",EDGE,"E67")])]})]});}
            var Q5;
            Q5=makeQuery(id+"F8.boolean.opBoolean","INTERSECT",EDGE,{"disambiguationData":[OD(0.0)],"derivedFrom":[makeQuery(id+"F5.opExtrude","SWEPT_FACE",FACE,{"disambiguationData":[OSD([sQuery(id+"F4.wireOp",EDGE,"E30")])]}),makeQuery(id+"F8.opExtrude","SWEPT_FACE",FACE,{"disambiguationData":[OSD([sQuery(id+"F7.wireOp",EDGE,"E67")])]})]});
            fillet(context, id + "F14", {"entities" : qUnion([Q0, Q1, Q2, Q3, Q4, Q5]), "radius" : 3 * mm, "tangentPropagation" : true, "allowEdgeOverflow" : false});
        }
        {
            var Q0;
            Q0=makeQuery(id+"F1.opExtrude","CAP_EDGE",EDGE,{"disambiguationData":[OSD([sQuery(id+"F0.wireOp",EDGE,"E1.bottom")])],"isStart":false});
            fillet(context, id + "F15", {"entities" : qUnion([Q0]), "radius" : 2 * mm, "tangentPropagation" : true, "allowEdgeOverflow" : false});
        }
        {
            var Q0;
            {var subQ0=sQuery(id+"F0.wireOp",EDGE,"E21.filletArc");var subQ1=sQuery(id+"F0.wireOp",EDGE,"E7");var subQ2=sQuery(id+"F0.wireOp",EDGE,"E6");var subQ3=sQuery(id+"F0.wireOp",EDGE,"E5");var subQ4=sQuery(id+"F0.wireOp",EDGE,"E4");var subQ5=sQuery(id+"F0.wireOp",EDGE,"E22.filletArc");var subQ6=sQuery(id+"F0.wireOp",EDGE,"E1.bottom");var subQ7=sQuery(id+"F0.wireOp",EDGE,"E1.right");var subQ8=sQuery(id+"F0.wireOp",EDGE,"E1.top");var subQ9=sQuery(id+"F0.wireOp",EDGE,"E1.left");var subQ10=sQuery(id+"F0.wireOp",EDGE,"E23.filletArc");var subQ11=sQuery(id+"F0.wireOp",EDGE,"E24.filletArc");Q0=makeQuery(id+"F2.boolean.opBoolean","SPLIT",FACE,{"disambiguationData":[TD([makeQuery(id+"F1.opExtrude","SWEPT_FACE",FACE,{"disambiguationData":[OSD([subQ6])]})])],"derivedFrom":makeQuery(id+"F1.opExtrude","CAP_FACE",FACE,{"disambiguationData":[OSD([subQ6,subQ8,subQ9,subQ7,subQ4,subQ3,subQ2,subQ1,subQ0,subQ5,subQ10,subQ11])],"isStart":true})});}
            var sketch = newSketch(context, id + "F16", { "sketchPlane" : qUnion([Q0])});
            skLineSegment(sketch, "E79", {"start": v(0, 90) * mm, "end": v(0, 120) * mm, "construction": true});
            skCircle(sketch, "E80", {"center": v(0, 120) * mm, "radius": 6 * mm});
            skArc(sketch, "E81", {"start": v(15, 120) * mm, "mid": v(0, 135) * mm, "end": v(-15, 120) * mm});
            skLineSegment(sketch, "E82", {"start": v(-15, 120) * mm, "end": v(-15, 108) * mm});
            skLineSegment(sketch, "E83", {"start": v(-15, 108) * mm, "end": v(-33, 90) * mm});
            skLineSegment(sketch, "E84", {"start": v(15, 120) * mm, "end": v(15, 108) * mm});
            skLineSegment(sketch, "E85", {"start": v(15, 108) * mm, "end": v(33, 90) * mm});
            skLineSegment(sketch, "E86", {"start": v(80, 0) * mm, "end": v(-80, 0) * mm, "construction": true});
            skArc(sketch, "E87.MirrorCS", {"start": v(15, -120) * mm, "mid": v(0, -135) * mm, "end": v(-15, -120) * mm});
            skLineSegment(sketch, "E88.MirrorCS", {"start": v(-15, -120) * mm, "end": v(-15, -108) * mm});
            skLineSegment(sketch, "E89.MirrorCS", {"start": v(-15, -108) * mm, "end": v(-33, -90) * mm});
            skLineSegment(sketch, "E90.MirrorCS", {"start": v(15, -108) * mm, "end": v(33, -90) * mm});
            skLineSegment(sketch, "E91.MirrorCS", {"start": v(15, -120) * mm, "end": v(15, -108) * mm});
            skCircle(sketch, "E92.MirrorC", {"center": v(0, -120) * mm, "radius": 6 * mm});
            skLineSegment(sketch, "E93.MirrorCS", {"start": v(0, -90) * mm, "end": v(0, -120) * mm, "construction": true});
            skSolve(sketch);
        }
        {
            var Q0;
            Q0=makeQuery(id+"F16.imprint","IMPRINT",FACE,{"disambiguationData":[TD([[makeQuery(id+"F16.imprint","IMPRINT",EDGE,{"derivedFrom":sQuery(id+"F16.wireOp",EDGE,"E80")}),-1.0]])]});
            var Q1;
            Q1=makeQuery(id+"F16.imprint","IMPRINT",FACE,{"disambiguationData":[TD([[makeQuery(id+"F16.imprint","IMPRINT",EDGE,{"derivedFrom":makeQuery(id+"F1.opExtrude","CAP_EDGE",EDGE,{"disambiguationData":[OSD([sQuery(id+"F0.wireOp",EDGE,"E1.left")])],"isStart":true})}),-1.0]])]});
            var Q2;
            Q2=makeQuery(id+"F16.imprint","IMPRINT",FACE,{"disambiguationData":[TD([[makeQuery(id+"F16.imprint","IMPRINT",EDGE,{"derivedFrom":sQuery(id+"F16.wireOp",EDGE,"E87.MirrorCS")}),-1.0]])]});
            var Q3;
            Q3=makeQuery(id+"F2.opExtrude","CAP_FACE",FACE,{"disambiguationData":[OSD([sQuery(id+"F0.wireOp",EDGE,"E12"),sQuery(id+"F0.wireOp",EDGE,"E13"),sQuery(id+"F0.wireOp",EDGE,"E14"),sQuery(id+"F0.wireOp",EDGE,"E15"),sQuery(id+"F0.wireOp",EDGE,"E17.filletArc"),sQuery(id+"F0.wireOp",EDGE,"E18.filletArc"),sQuery(id+"F0.wireOp",EDGE,"E19.filletArc"),sQuery(id+"F0.wireOp",EDGE,"E20.filletArc"),sQuery(id+"F0.wireOp",EDGE,"E25.0"),sQuery(id+"F0.wireOp",EDGE,"E25.1"),sQuery(id+"F0.wireOp",EDGE,"E25.2"),sQuery(id+"F0.wireOp",EDGE,"E25.3"),sQuery(id+"F0.wireOp",EDGE,"E25.4"),sQuery(id+"F0.wireOp",EDGE,"E25.5"),sQuery(id+"F0.wireOp",EDGE,"E25.6"),sQuery(id+"F0.wireOp",EDGE,"E25.7")])],"isStart":false});
            extrude(context, id + "F17", {"entities" : qUnion([Q0, Q1, Q2]), "endBound" : BoundingType.UP_TO_SURFACE, "endBoundEntityFace" : qUnion([Q3]), "depth" : 25 * mm});
        }
    });
